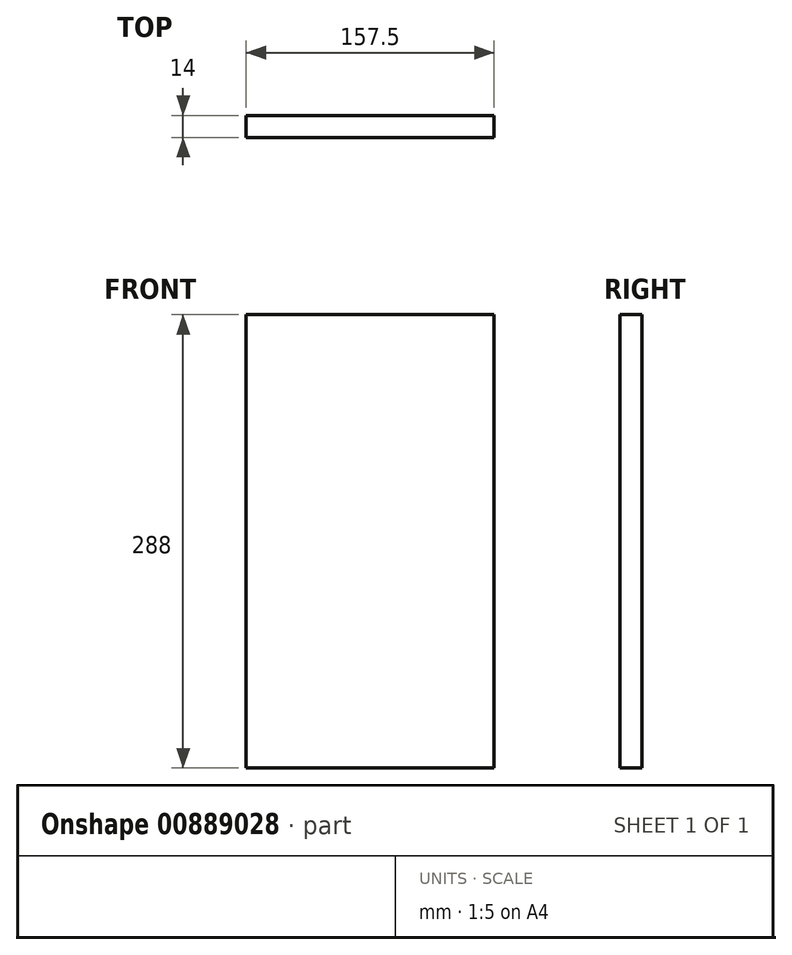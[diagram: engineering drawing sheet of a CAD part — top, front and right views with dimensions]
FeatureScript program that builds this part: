
annotation { "Feature Type Name" : "Feature", "Feature Type Description" : "" }
export const myFeature = defineFeature(function(context is Context, id is Id, definition is map)
    precondition{}
    {
        {
            var Q0;
            Q0=qCreatedBy(makeId("Right.planeOp"),FACE);
            var sketch = newSketch(context, id + "F0", { "sketchPlane" : qUnion([Q0])});
            skLineSegment(sketch, "E0.bottom", {"start": v(-7, 144) * mm, "end": v(7, 144) * mm});
            skLineSegment(sketch, "E0.top", {"start": v(-7, -144) * mm, "end": v(7, -144) * mm});
            skLineSegment(sketch, "E0.left", {"start": v(-7, 144) * mm, "end": v(-7, -144) * mm});
            skLineSegment(sketch, "E0.right", {"start": v(7, 144) * mm, "end": v(7, -144) * mm});
            skPoint(sketch, "E0.middle", {"position": v(0, 0) * mm});
            skSolve(sketch);
        }
        {
            var Q0;
            Q0=qSketchRegion(id+"F0",true);
            extrude(context, id + "F1", {"entities" : qUnion([Q0]), "endBound" : BoundingType.SYMMETRIC, "depth" : 157.5 * mm, "offsetDistance" : 25 * mm});
        }
    });
